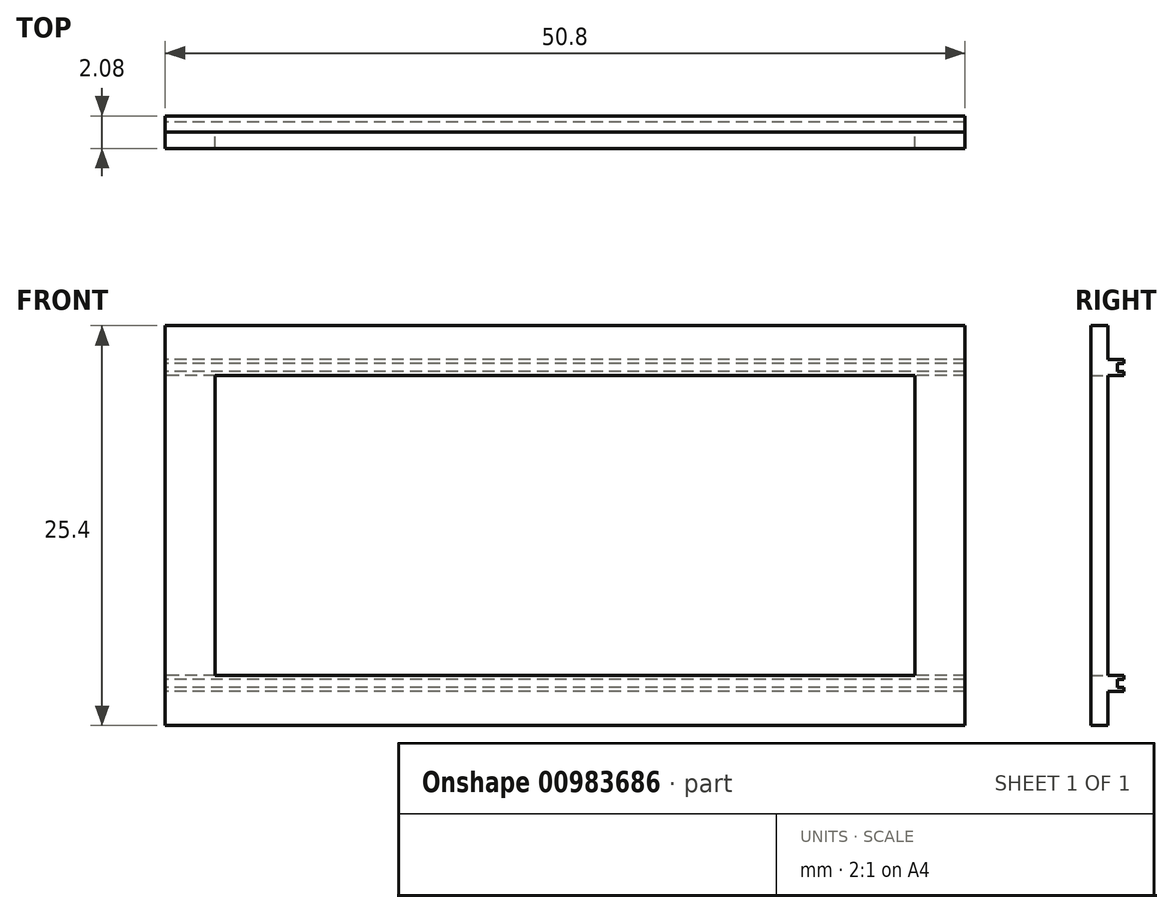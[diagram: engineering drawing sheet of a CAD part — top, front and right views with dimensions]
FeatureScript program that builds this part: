
annotation { "Feature Type Name" : "Feature", "Feature Type Description" : "" }
export const myFeature = defineFeature(function(context is Context, id is Id, definition is map)
    precondition{}
    {
        {
            var Q0;
            Q0=qCreatedBy(makeId("Front.planeOp"),FACE);
            var sketch = newSketch(context, id + "F0", { "sketchPlane" : qUnion([Q0])});
            skLineSegment(sketch, "E0.bottom", {"start": v(25.4, 12.7) * mm, "end": v(-25.4, 12.7) * mm});
            skLineSegment(sketch, "E0.top", {"start": v(25.4, -12.7) * mm, "end": v(-25.4, -12.7) * mm});
            skLineSegment(sketch, "E0.left", {"start": v(25.4, 12.7) * mm, "end": v(25.4, -12.7) * mm});
            skLineSegment(sketch, "E0.right", {"start": v(-25.4, 12.7) * mm, "end": v(-25.4, -12.7) * mm});
            skPoint(sketch, "E0.middle", {"position": v(0, 0) * mm});
            skLineSegment(sketch, "E1.bottom", {"start": v(22.22, 9.53) * mm, "end": v(-22.23, 9.53) * mm});
            skLineSegment(sketch, "E1.top", {"start": v(22.23, -9.53) * mm, "end": v(-22.22, -9.53) * mm});
            skLineSegment(sketch, "E1.left", {"start": v(22.23, 9.53) * mm, "end": v(22.23, -9.53) * mm});
            skLineSegment(sketch, "E1.right", {"start": v(-22.23, 9.53) * mm, "end": v(-22.22, -9.53) * mm});
            skSolve(sketch);
        }
        {
            var Q0;
            Q0 = qSketchRegion(id + "F0", true);
            extrude(context, id + "F1", {"entities" : qUnion([Q0]), "depth" : 1.06 * mm, "offsetDistance" : 25.4 * mm});
        }
        {
            var Q0;
            Q0=qCreatedBy(makeId("Right.planeOp"),FACE);
            var sketch = newSketch(context, id + "F2", { "sketchPlane" : qUnion([Q0])});
            skLineSegment(sketch, "E2.bottom", {"start": v(0, 9.53) * mm, "end": v(0, 9.53) * mm});
            skLineSegment(sketch, "E2.top", {"start": v(0, -9.53) * mm, "end": v(0, -9.53) * mm});
            skLineSegment(sketch, "E2.left", {"start": v(0, 0) * mm, "end": v(0, -9.52) * mm});
            skLineSegment(sketch, "E2.right", {"start": v(0, 0) * mm, "end": v(0, -9.52) * mm});
            skPoint(sketch, "E2.middle", {"position": v(0, 0) * mm});
            skLineSegment(sketch, "E3", {"start": v(0, 9.53) * mm, "end": v(1.02, 9.53) * mm});
            skLineSegment(sketch, "E4", {"start": v(1.02, 9.53) * mm, "end": v(1.02, 9.78) * mm});
            skLineSegment(sketch, "E5", {"start": v(1.02, 9.78) * mm, "end": v(0.63, 9.78) * mm});
            skLineSegment(sketch, "E6", {"start": v(0.63, 9.78) * mm, "end": v(0.63, 10.29) * mm});
            skLineSegment(sketch, "E7", {"start": v(0.63, 10.29) * mm, "end": v(1.02, 10.29) * mm});
            skLineSegment(sketch, "E8", {"start": v(1.02, 10.29) * mm, "end": v(1.02, 10.54) * mm});
            skLineSegment(sketch, "E9", {"start": v(1.02, 10.54) * mm, "end": v(0, 10.54) * mm});
            skLineSegment(sketch, "E10", {"start": v(0, 10.54) * mm, "end": v(0, 9.53) * mm});
            skLineSegment(sketch, "E11.bottom", {"start": v(2.12, -11.8) * mm, "end": v(2.12, -11.8) * mm});
            skLineSegment(sketch, "E12", {"start": v(0, -10.54) * mm, "end": v(1.02, -10.54) * mm});
            skLineSegment(sketch, "E13", {"start": v(1.02, -10.54) * mm, "end": v(1.02, -10.29) * mm});
            skLineSegment(sketch, "E14", {"start": v(1.02, -10.29) * mm, "end": v(0.63, -10.29) * mm});
            skLineSegment(sketch, "E15", {"start": v(0.63, -10.29) * mm, "end": v(0.63, -9.78) * mm});
            skLineSegment(sketch, "E16", {"start": v(0.63, -9.78) * mm, "end": v(1.02, -9.78) * mm});
            skLineSegment(sketch, "E17", {"start": v(1.02, -9.78) * mm, "end": v(1.02, -9.53) * mm});
            skLineSegment(sketch, "E18", {"start": v(1.02, -9.53) * mm, "end": v(0, -9.53) * mm});
            skLineSegment(sketch, "E19", {"start": v(0, -9.53) * mm, "end": v(0, -10.54) * mm});
            skSolve(sketch);
        }
        {
            var Q0;
            Q0 = qSketchRegion(id + "F2", true);
            extrude(context, id + "F3", {"entities" : qUnion([Q0]), "operationType" : NewBodyOperationType.ADD, "endBound" : BoundingType.SYMMETRIC, "depth" : 50.8 * mm, "offsetDistance" : 25.4 * mm});
        }
    });
